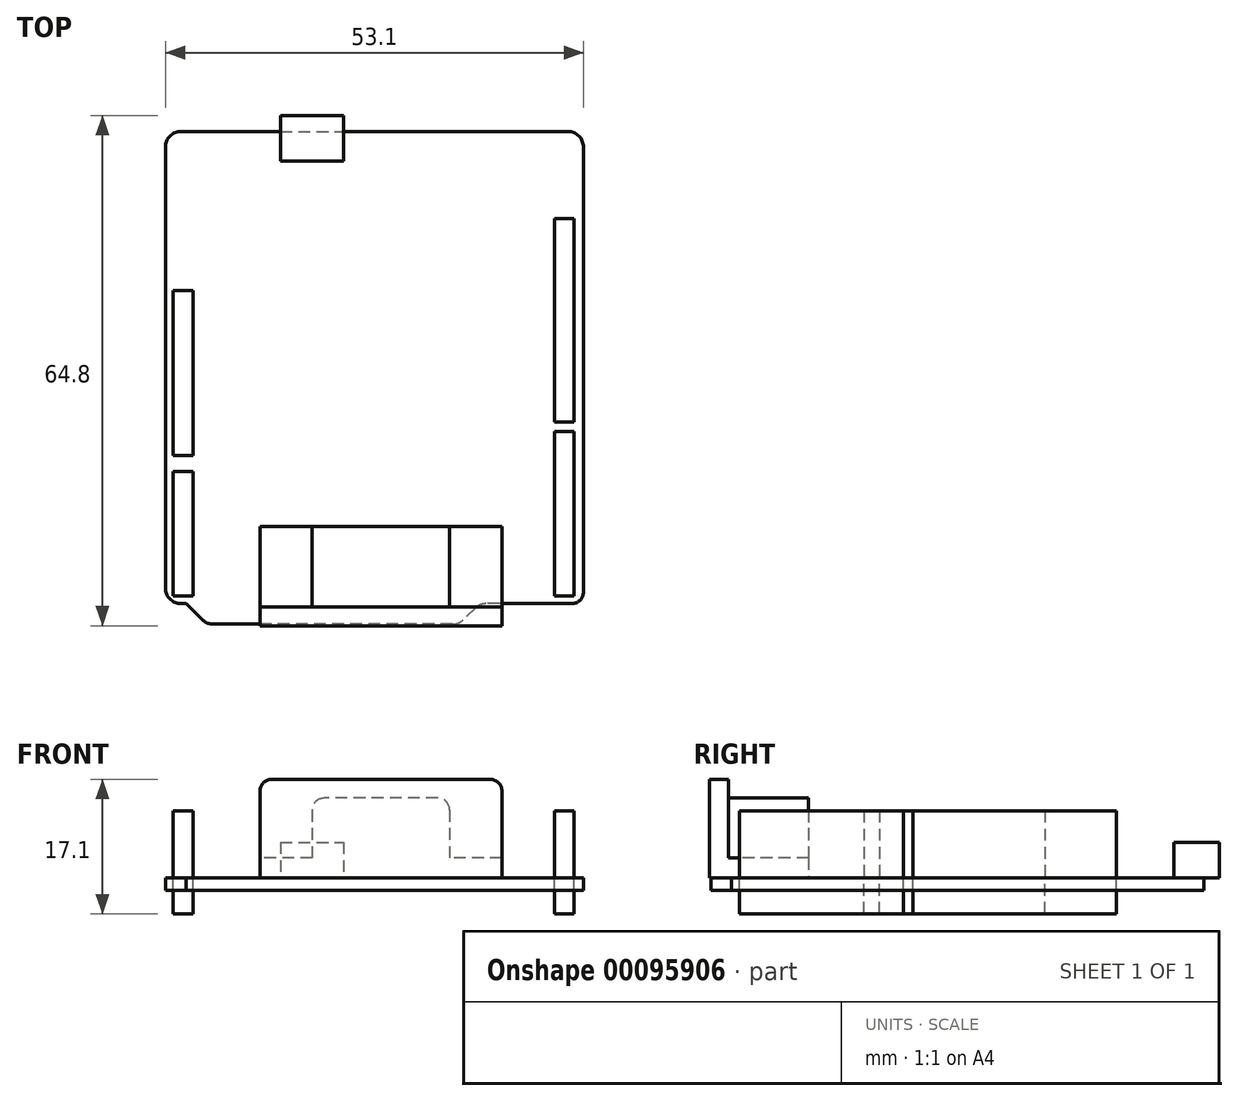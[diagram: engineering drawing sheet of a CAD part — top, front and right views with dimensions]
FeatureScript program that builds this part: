
annotation { "Feature Type Name" : "Feature", "Feature Type Description" : "" }
export const myFeature = defineFeature(function(context is Context, id is Id, definition is map)
    precondition{}
    {
        {
            var Q0;
            Q0=qCreatedBy(makeId("Top.planeOp"),FACE);
            var sketch = newSketch(context, id + "F0", { "sketchPlane" : qUnion([Q0])});
            skLineSegment(sketch, "E0", {"start": v(-21.1, 31.3) * mm, "end": v(28, 31.3) * mm});
            skLineSegment(sketch, "E1", {"start": v(30, 29.3) * mm, "end": v(30, -27.2) * mm});
            skLineSegment(sketch, "E2", {"start": v(28.5, -28.7) * mm, "end": v(17.63, -28.7) * mm});
            skLineSegment(sketch, "E3", {"start": v(16.21, -29.29) * mm, "end": v(14.79, -30.71) * mm});
            skLineSegment(sketch, "E4", {"start": v(13.37, -31.3) * mm, "end": v(-17.02, -31.3) * mm});
            skLineSegment(sketch, "E5", {"start": v(-18.44, -30.71) * mm, "end": v(-20.45, -28.7) * mm});
            skLineSegment(sketch, "E6", {"start": v(-20.45, -28.7) * mm, "end": v(-21.1, -28.7) * mm});
            skLineSegment(sketch, "E7", {"start": v(-23.1, -26.7) * mm, "end": v(-23.1, 29.3) * mm});
            skPoint(sketch, "E8.visualSharp", {"position": v(-23.1, 31.3) * mm});
            skArc(sketch, "E8.filletArc", {"start": v(-21.1, 31.3) * mm, "mid": v(-22.51, 30.71) * mm, "end": v(-23.1, 29.3) * mm});
            skPoint(sketch, "E9.visualSharp", {"position": v(30, 31.3) * mm});
            skArc(sketch, "E9.filletArc", {"start": v(30, 29.3) * mm, "mid": v(29.41, 30.71) * mm, "end": v(28, 31.3) * mm});
            skPoint(sketch, "E10.visualSharp", {"position": v(-23.1, -28.7) * mm});
            skArc(sketch, "E10.filletArc", {"start": v(-23.1, -26.7) * mm, "mid": v(-22.51, -28.11) * mm, "end": v(-21.1, -28.7) * mm});
            skPoint(sketch, "E11.visualSharp", {"position": v(-17.85, -31.3) * mm});
            skArc(sketch, "E11.filletArc", {"start": v(-18.44, -30.71) * mm, "mid": v(-17.79, -31.15) * mm, "end": v(-17.02, -31.3) * mm});
            skPoint(sketch, "E12.visualSharp", {"position": v(14.2, -31.3) * mm});
            skArc(sketch, "E12.filletArc", {"start": v(13.37, -31.3) * mm, "mid": v(14.14, -31.15) * mm, "end": v(14.79, -30.71) * mm});
            skPoint(sketch, "E13.visualSharp", {"position": v(16.8, -28.7) * mm});
            skArc(sketch, "E13.filletArc", {"start": v(17.63, -28.7) * mm, "mid": v(16.86, -28.85) * mm, "end": v(16.21, -29.29) * mm});
            skPoint(sketch, "E14.visualSharp", {"position": v(30, -28.7) * mm});
            skArc(sketch, "E14.filletArc", {"start": v(28.5, -28.7) * mm, "mid": v(29.56, -28.26) * mm, "end": v(30, -27.2) * mm});
            skSolve(sketch);
        }
        {
            var Q0;
            Q0=qSketchRegion(id+"F0",true);
            extrude(context, id + "F1", {"entities" : qUnion([Q0]), "depth" : 1.6 * mm});
        }
        {
            var Q0;
            Q0=makeQuery(id+"F1.opExtrude","CAP_FACE",FACE,{"disambiguationData":[OSD([sQuery(id+"F0.wireOp",EDGE,"E0"),sQuery(id+"F0.wireOp",EDGE,"E1"),sQuery(id+"F0.wireOp",EDGE,"E2"),sQuery(id+"F0.wireOp",EDGE,"E3"),sQuery(id+"F0.wireOp",EDGE,"E4"),sQuery(id+"F0.wireOp",EDGE,"E5"),sQuery(id+"F0.wireOp",EDGE,"E6"),sQuery(id+"F0.wireOp",EDGE,"E7"),sQuery(id+"F0.wireOp",EDGE,"E8.filletArc"),sQuery(id+"F0.wireOp",EDGE,"E9.filletArc"),sQuery(id+"F0.wireOp",EDGE,"E10.filletArc"),sQuery(id+"F0.wireOp",EDGE,"E11.filletArc"),sQuery(id+"F0.wireOp",EDGE,"E12.filletArc"),sQuery(id+"F0.wireOp",EDGE,"E13.filletArc"),sQuery(id+"F0.wireOp",EDGE,"E14.filletArc")])],"isStart":false});
            var sketch = newSketch(context, id + "F2", { "sketchPlane" : qUnion([Q0])});
            skLineSegment(sketch, "E15.bottom", {"start": v(28.8, 20.2) * mm, "end": v(26.3, 20.2) * mm});
            skLineSegment(sketch, "E15.top", {"start": v(28.8, -5.65) * mm, "end": v(26.3, -5.65) * mm});
            skLineSegment(sketch, "E15.left", {"start": v(28.8, 20.2) * mm, "end": v(28.8, -5.65) * mm});
            skLineSegment(sketch, "E15.right", {"start": v(26.3, 20.2) * mm, "end": v(26.3, -5.65) * mm});
            skLineSegment(sketch, "E16.bottom", {"start": v(28.8, -6.85) * mm, "end": v(26.3, -6.85) * mm});
            skLineSegment(sketch, "E16.top", {"start": v(28.8, -27.7) * mm, "end": v(26.3, -27.7) * mm});
            skLineSegment(sketch, "E16.left", {"start": v(28.8, -6.85) * mm, "end": v(28.8, -27.7) * mm});
            skLineSegment(sketch, "E16.right", {"start": v(26.3, -6.85) * mm, "end": v(26.3, -27.7) * mm});
            skLineSegment(sketch, "E17.bottom", {"start": v(-19.6, 11.1) * mm, "end": v(-22.1, 11.1) * mm});
            skLineSegment(sketch, "E17.top", {"start": v(-19.6, -9.9) * mm, "end": v(-22.1, -9.9) * mm});
            skLineSegment(sketch, "E17.left", {"start": v(-19.6, 11.1) * mm, "end": v(-19.6, -9.9) * mm});
            skLineSegment(sketch, "E17.right", {"start": v(-22.1, 11.1) * mm, "end": v(-22.1, -9.9) * mm});
            skLineSegment(sketch, "E18.bottom", {"start": v(-19.6, -11.9) * mm, "end": v(-22.1, -11.9) * mm});
            skLineSegment(sketch, "E18.top", {"start": v(-19.6, -27.7) * mm, "end": v(-22.1, -27.7) * mm});
            skLineSegment(sketch, "E18.left", {"start": v(-19.6, -11.9) * mm, "end": v(-19.6, -27.7) * mm});
            skLineSegment(sketch, "E18.right", {"start": v(-22.1, -11.9) * mm, "end": v(-22.1, -27.7) * mm});
            skSolve(sketch);
        }
        {
            var Q0;
            Q0=qSketchRegion(id+"F2",true);
            extrude(context, id + "F3", {"entities" : qUnion([Q0]), "depth" : 8.5 * mm});
        }
        {
            var Q0;
            Q0=qSketchRegion(id+"F2",true);
            extrude(context, id + "F4", {"entities" : qUnion([Q0]), "oppositeDirection" : true, "depth" : 4.6 * mm});
        }
        {
            var Q0;
            Q0=makeQuery(id+"F1.opExtrude","CAP_FACE",FACE,{"disambiguationData":[OSD([sQuery(id+"F0.wireOp",EDGE,"E0"),sQuery(id+"F0.wireOp",EDGE,"E1"),sQuery(id+"F0.wireOp",EDGE,"E2"),sQuery(id+"F0.wireOp",EDGE,"E3"),sQuery(id+"F0.wireOp",EDGE,"E4"),sQuery(id+"F0.wireOp",EDGE,"E5"),sQuery(id+"F0.wireOp",EDGE,"E6"),sQuery(id+"F0.wireOp",EDGE,"E7"),sQuery(id+"F0.wireOp",EDGE,"E8.filletArc"),sQuery(id+"F0.wireOp",EDGE,"E9.filletArc"),sQuery(id+"F0.wireOp",EDGE,"E10.filletArc"),sQuery(id+"F0.wireOp",EDGE,"E11.filletArc"),sQuery(id+"F0.wireOp",EDGE,"E12.filletArc"),sQuery(id+"F0.wireOp",EDGE,"E13.filletArc"),sQuery(id+"F0.wireOp",EDGE,"E14.filletArc")])],"isStart":false});
            var sketch = newSketch(context, id + "F5", { "sketchPlane" : qUnion([Q0])});
            skLineSegment(sketch, "E19.bottom", {"start": v(-8.5, 27.5) * mm, "end": v(-0.5, 27.5) * mm});
            skLineSegment(sketch, "E19.top", {"start": v(-8.5, 33.3) * mm, "end": v(-0.5, 33.3) * mm});
            skLineSegment(sketch, "E19.left", {"start": v(-8.5, 27.5) * mm, "end": v(-8.5, 33.3) * mm});
            skLineSegment(sketch, "E19.right", {"start": v(-0.5, 27.5) * mm, "end": v(-0.5, 33.3) * mm});
            skSolve(sketch);
        }
        {
            var Q0;
            Q0=qSketchRegion(id+"F5",true);
            extrude(context, id + "F6", {"entities" : qUnion([Q0]), "depth" : 4.5 * mm});
        }
        {
            var Q0;
            Q0=makeQuery(id+"F1.opExtrude","CAP_FACE",FACE,{"disambiguationData":[OSD([sQuery(id+"F0.wireOp",EDGE,"E0"),sQuery(id+"F0.wireOp",EDGE,"E1"),sQuery(id+"F0.wireOp",EDGE,"E2"),sQuery(id+"F0.wireOp",EDGE,"E3"),sQuery(id+"F0.wireOp",EDGE,"E4"),sQuery(id+"F0.wireOp",EDGE,"E5"),sQuery(id+"F0.wireOp",EDGE,"E6"),sQuery(id+"F0.wireOp",EDGE,"E7"),sQuery(id+"F0.wireOp",EDGE,"E8.filletArc"),sQuery(id+"F0.wireOp",EDGE,"E9.filletArc"),sQuery(id+"F0.wireOp",EDGE,"E10.filletArc"),sQuery(id+"F0.wireOp",EDGE,"E11.filletArc"),sQuery(id+"F0.wireOp",EDGE,"E12.filletArc"),sQuery(id+"F0.wireOp",EDGE,"E13.filletArc"),sQuery(id+"F0.wireOp",EDGE,"E14.filletArc")])],"isStart":false});
            var sketch = newSketch(context, id + "F7", { "sketchPlane" : qUnion([Q0])});
            skLineSegment(sketch, "E20.bottom", {"start": v(19.65, -18.9) * mm, "end": v(-11.1, -18.9) * mm});
            skLineSegment(sketch, "E20.top", {"start": v(19.65, -31.5) * mm, "end": v(-11.1, -31.5) * mm});
            skLineSegment(sketch, "E20.left", {"start": v(19.65, -18.9) * mm, "end": v(19.65, -31.5) * mm});
            skLineSegment(sketch, "E20.right", {"start": v(-11.1, -18.9) * mm, "end": v(-11.1, -31.5) * mm});
            skSolve(sketch);
        }
        {
            var Q0;
            Q0=qSketchRegion(id+"F7",true);
            extrude(context, id + "F8", {"entities" : qUnion([Q0]), "operationType" : NewBodyOperationType.ADD, "depth" : 12.5 * mm});
        }
        {
            var Q0;
            Q0=makeQuery(id+"F8.opExtrude","CAP_FACE",FACE,{"disambiguationData":[OSD([sQuery(id+"F7.wireOp",EDGE,"E20.bottom"),sQuery(id+"F7.wireOp",EDGE,"E20.top"),sQuery(id+"F7.wireOp",EDGE,"E20.left"),sQuery(id+"F7.wireOp",EDGE,"E20.right")])],"isStart":false});
            var sketch = newSketch(context, id + "F9", { "sketchPlane" : qUnion([Q0])});
            skLineSegment(sketch, "E21.bottom", {"start": v(19.65, -18.9) * mm, "end": v(-11.1, -18.9) * mm});
            skLineSegment(sketch, "E21.top", {"start": v(19.65, -29.1) * mm, "end": v(-11.1, -29.1) * mm});
            skLineSegment(sketch, "E21.left", {"start": v(19.65, -18.9) * mm, "end": v(19.65, -29.1) * mm});
            skLineSegment(sketch, "E21.right", {"start": v(-11.1, -18.9) * mm, "end": v(-11.1, -29.1) * mm});
            skSolve(sketch);
        }
        {
            var Q0;
            Q0=qSketchRegion(id+"F9",true);
            extrude(context, id + "F10", {"entities" : qUnion([Q0]), "operationType" : NewBodyOperationType.REMOVE, "oppositeDirection" : true, "depth" : 10 * mm});
        }
        {
            var Q0;
            Q0=makeQuery(id+"F10.boolean.opBoolean","COPY",FACE,{"derivedFrom":makeQuery(id+"F10.opExtrude","CAP_FACE",FACE,{"disambiguationData":[OSD([sQuery(id+"F9.wireOp",EDGE,"E21.bottom"),sQuery(id+"F9.wireOp",EDGE,"E21.top"),sQuery(id+"F9.wireOp",EDGE,"E21.left"),sQuery(id+"F9.wireOp",EDGE,"E21.right")])],"isStart":false})});
            var sketch = newSketch(context, id + "F11", { "sketchPlane" : qUnion([Q0])});
            skLineSegment(sketch, "E22.bottom", {"start": v(13, -18.9) * mm, "end": v(-4.45, -18.9) * mm});
            skLineSegment(sketch, "E22.top", {"start": v(13, -29.1) * mm, "end": v(-4.45, -29.1) * mm});
            skLineSegment(sketch, "E22.left", {"start": v(13, -18.9) * mm, "end": v(13, -29.1) * mm});
            skLineSegment(sketch, "E22.right", {"start": v(-4.45, -18.9) * mm, "end": v(-4.45, -29.1) * mm});
            skSolve(sketch);
        }
        {
            var Q0;
            Q0=qSketchRegion(id+"F11",true);
            extrude(context, id + "F12", {"entities" : qUnion([Q0]), "operationType" : NewBodyOperationType.ADD, "depth" : 7.6 * mm});
        }
        {
            var Q0;
            Q0=makeQuery(id+"F12.opExtrude","CAP_EDGE",EDGE,{"disambiguationData":[OSD([sQuery(id+"F11.wireOp",EDGE,"E22.right")])],"isStart":false});
            var Q1;
            Q1=makeQuery(id+"F12.opExtrude","CAP_EDGE",EDGE,{"disambiguationData":[OSD([sQuery(id+"F11.wireOp",EDGE,"E22.left")])],"isStart":false});
            var Q2;
            Q2=makeQuery(id+"F8.opExtrude","CAP_EDGE",EDGE,{"disambiguationData":[OSD([sQuery(id+"F7.wireOp",EDGE,"E20.left")])],"isStart":false});
            var Q3;
            Q3=makeQuery(id+"F8.opExtrude","CAP_EDGE",EDGE,{"disambiguationData":[OSD([sQuery(id+"F7.wireOp",EDGE,"E20.right")])],"isStart":false});
            fillet(context, id + "F13", {"entities" : qUnion([Q0, Q1, Q2, Q3]), "radius" : 1.5 * mm, "tangentPropagation" : true, "allowEdgeOverflow" : false});
        }
    });
